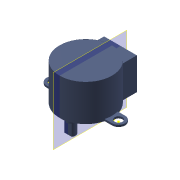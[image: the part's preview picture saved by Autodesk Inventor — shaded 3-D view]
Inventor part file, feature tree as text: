
AUTODESK INVENTOR PART (.ipt)
format: ipt  version: 2019.4 (Build 234330000, 330)  size: 210,432 bytes
history: native  units: mm
features: other x2, sketch x1, plane x1
ambient origin geometry x8: Origin, YZ Plane, XZ Plane, XY Plane, X Axis, Y Axis, Z Axis, Center Point
bodies: Body1 (feature_tree), Body2 (feature_tree), Body3 (feature_tree), Body4 (feature_tree), Body5 (feature_tree), Body6 (feature_tree), Body7 (feature_tree), Body8 (feature_tree), Body9 (feature_tree), Body10 (feature_tree), Body11 (feature_tree), Body12 (feature_tree), Body13 (feature_tree), Body14 (feature_tree), Body15 (feature_tree), Body16 (feature_tree), Body17 (feature_tree), Body18 (feature_tree), Body19 (feature_tree), Body20 (feature_tree), Body21 (feature_tree), Body22 (feature_tree), Body23 (feature_tree), Body24 (feature_tree), Body25 (feature_tree), Body26 (feature_tree), Body27 (feature_tree), Body28 (feature_tree), Body29 (feature_tree), Body30 (feature_tree), Body31 (feature_tree)
feature tree (4):
  sketch  "Skizze1"
  plane  "Work Plane1"
  other  "Zusammengesetzt1"
  other  "Fläche1"
